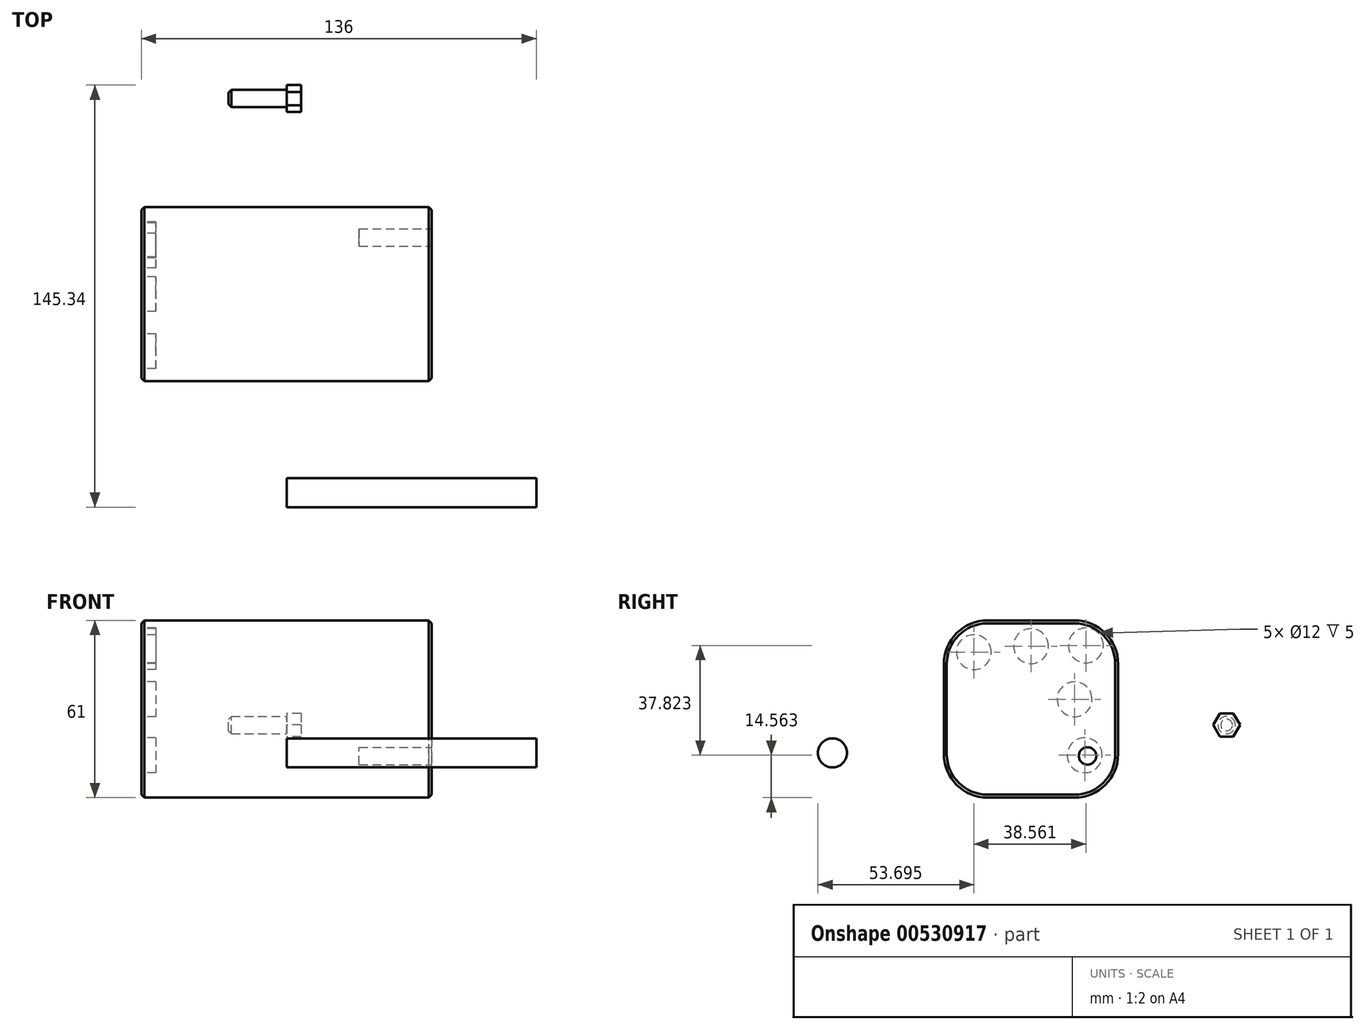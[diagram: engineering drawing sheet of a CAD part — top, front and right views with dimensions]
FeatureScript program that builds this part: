
annotation { "Feature Type Name" : "Feature", "Feature Type Description" : "" }
export const myFeature = defineFeature(function(context is Context, id is Id, definition is map)
    precondition{}
    {
        {
            var Q0;
            Q0=qCreatedBy(makeId("Top.planeOp"),FACE);
            var sketch = newSketch(context, id + "F0", { "sketchPlane" : qUnion([Q0])});
            skLineSegment(sketch, "E0.bottom", {"start": v(50, -30) * mm, "end": v(-50, -30) * mm});
            skLineSegment(sketch, "E0.top", {"start": v(50, 30) * mm, "end": v(-50, 30) * mm});
            skLineSegment(sketch, "E0.left", {"start": v(50, -30) * mm, "end": v(50, 30) * mm});
            skLineSegment(sketch, "E0.right", {"start": v(-50, -30) * mm, "end": v(-50, 30) * mm});
            skPoint(sketch, "E0.middle", {"position": v(0, 0) * mm});
            skSolve(sketch);
        }
        {
            var Q0;
            Q0 = qSketchRegion(id + "F0", true);
            extrude(context, id + "F1", {"entities" : qUnion([Q0]), "depth" : 61 * mm, "offsetDistance" : 25 * mm});
        }
        {
            var Q0;
            Q0=makeQuery(id+"F1.opExtrude","CAP_EDGE",EDGE,{"disambiguationData":[OSD([sQuery(id+"F0.wireOp",EDGE,"E0.bottom")])],"isStart":false});
            var Q1;
            Q1=makeQuery(id+"F1.opExtrude","CAP_EDGE",EDGE,{"disambiguationData":[OSD([sQuery(id+"F0.wireOp",EDGE,"E0.top")])],"isStart":false});
            var Q2;
            Q2=makeQuery(id+"F1.opExtrude","CAP_EDGE",EDGE,{"disambiguationData":[OSD([sQuery(id+"F0.wireOp",EDGE,"E0.bottom")])],"isStart":true});
            var Q3;
            Q3=makeQuery(id+"F1.opExtrude","CAP_EDGE",EDGE,{"disambiguationData":[OSD([sQuery(id+"F0.wireOp",EDGE,"E0.top")])],"isStart":true});
            fillet(context, id + "F2", {"entities" : qUnion([Q0, Q1, Q2, Q3]), "radius" : 15 * mm, "tangentPropagation" : true, "allowEdgeOverflow" : false});
        }
        {
            var Q0;
            Q0=qCreatedBy(makeId("Right.planeOp"),FACE);
            var sketch = newSketch(context, id + "F3", { "sketchPlane" : qUnion([Q0])});
            skCircle(sketch, "E1", {"center": v(-68.37, 15.37) * mm, "radius": 5 * mm});
            skSolve(sketch);
        }
        {
            var Q0;
            Q0 = qSketchRegion(id + "F3", true);
            extrude(context, id + "F4", {"entities" : qUnion([Q0]), "depth" : 86 * mm, "offsetDistance" : 25 * mm});
        }
        {
            var Q0;
            Q0=makeQuery(id+"F1.opExtrude","SWEPT_FACE",FACE,{"disambiguationData":[OSD([sQuery(id+"F0.wireOp",EDGE,"E0.right")])]});
            var sketch = newSketch(context, id + "F5", { "sketchPlane" : qUnion([Q0])});
            skCircle(sketch, "E2", {"center": v(-18.89, 52.39) * mm, "radius": 6 * mm});
            skCircle(sketch, "E3", {"center": v(-15, 33.84) * mm, "radius": 6 * mm});
            skCircle(sketch, "E4", {"center": v(19.67, 50.08) * mm, "radius": 6 * mm});
            skCircle(sketch, "E5", {"center": v(0, 52.15) * mm, "radius": 6 * mm});
            skCircle(sketch, "E6", {"center": v(-18.5, 14.56) * mm, "radius": 6 * mm});
            skSolve(sketch);
        }
        {
            var Q0;
            Q0 = qSketchRegion(id + "F5", true);
            extrude(context, id + "F6", {"entities" : qUnion([Q0]), "operationType" : NewBodyOperationType.REMOVE, "oppositeDirection" : true, "depth" : 5 * mm, "offsetDistance" : 25 * mm});
        }
        {
            var Q0;
            Q0=makeQuery(id+"F1.opExtrude","SWEPT_FACE",FACE,{"disambiguationData":[OSD([sQuery(id+"F0.wireOp",EDGE,"E0.left")])]});
            var sketch = newSketch(context, id + "F7", { "sketchPlane" : qUnion([Q0])});
            skCircle(sketch, "E7", {"center": v(19.46, 14.33) * mm, "radius": 3 * mm});
            skSolve(sketch);
        }
        {
            var Q0;
            Q0 = qSketchRegion(id + "F7", true);
            extrude(context, id + "F8", {"entities" : qUnion([Q0]), "operationType" : NewBodyOperationType.REMOVE, "oppositeDirection" : true, "depth" : 25 * mm, "offsetDistance" : 25 * mm});
        }
        {
            var Q0;
            Q0=qCreatedBy(makeId("Right.planeOp"),FACE);
            var sketch = newSketch(context, id + "F9", { "sketchPlane" : qUnion([Q0])});
            skCircle(sketch, "E8", {"center": v(67.35, 24.98) * mm, "radius": 3 * mm});
            skSolve(sketch);
        }
        {
            var Q0;
            Q0 = qSketchRegion(id + "F9", true);
            extrude(context, id + "F10", {"entities" : qUnion([Q0]), "oppositeDirection" : true, "depth" : 20 * mm, "offsetDistance" : 25 * mm});
        }
        {
            var Q0;
            Q0=makeQuery(id+"F10.opExtrude","CAP_FACE",FACE,{"disambiguationData":[OSD([sQuery(id+"F9.wireOp",EDGE,"E8")])],"isStart":true});
            var sketch = newSketch(context, id + "F11", { "sketchPlane" : qUnion([Q0])});
            skCircle(sketch, "E9.cCircle", {"center": v(67.35, 24.98) * mm, "radius": 4 * mm, "construction": true});
            skLineSegment(sketch, "E9.0", {"start": v(71.97, 24.98) * mm, "end": v(69.66, 20.98) * mm});
            skLineSegment(sketch, "E9.1", {"start": v(69.66, 20.98) * mm, "end": v(65.04, 20.98) * mm});
            skLineSegment(sketch, "E9.2", {"start": v(65.04, 20.98) * mm, "end": v(62.73, 24.98) * mm});
            skLineSegment(sketch, "E9.3", {"start": v(62.73, 24.98) * mm, "end": v(65.04, 28.98) * mm});
            skLineSegment(sketch, "E9.4", {"start": v(65.04, 28.98) * mm, "end": v(69.66, 28.98) * mm});
            skLineSegment(sketch, "E9.5", {"start": v(69.66, 28.98) * mm, "end": v(71.97, 24.98) * mm});
            skPoint(sketch, "E9.0.midPoint", {"position": v(70.82, 22.98) * mm});
            skSolve(sketch);
        }
        {
            var Q0;
            Q0 = qSketchRegion(id + "F11", true);
            extrude(context, id + "F12", {"entities" : qUnion([Q0]), "operationType" : NewBodyOperationType.ADD, "depth" : 5 * mm, "offsetDistance" : 25 * mm});
        }
        {
            var Q0;
            Q0=makeQuery(id+"F10.opExtrude","CAP_EDGE",EDGE,{"disambiguationData":[OSD([sQuery(id+"F9.wireOp",EDGE,"E8")])],"isStart":false});
            var Q1;
            {var subQ0=sQuery(id+"F0.wireOp",EDGE,"E0.top");Q1=makeQuery(id+"F2.opFillet","BLEND_FACE",FACE,{"disambiguationData":[OSD([subQ0]),TDD([makeQuery(id+"F1.opExtrude","CAP_EDGE",EDGE,{"disambiguationData":[OSD([subQ0])],"isStart":false})])]});}
            chamfer(context, id + "F13", {"entities" : qUnion([Q0, Q1]), "width" : 1 * mm, "tangentPropagation" : true});
        }
    });
